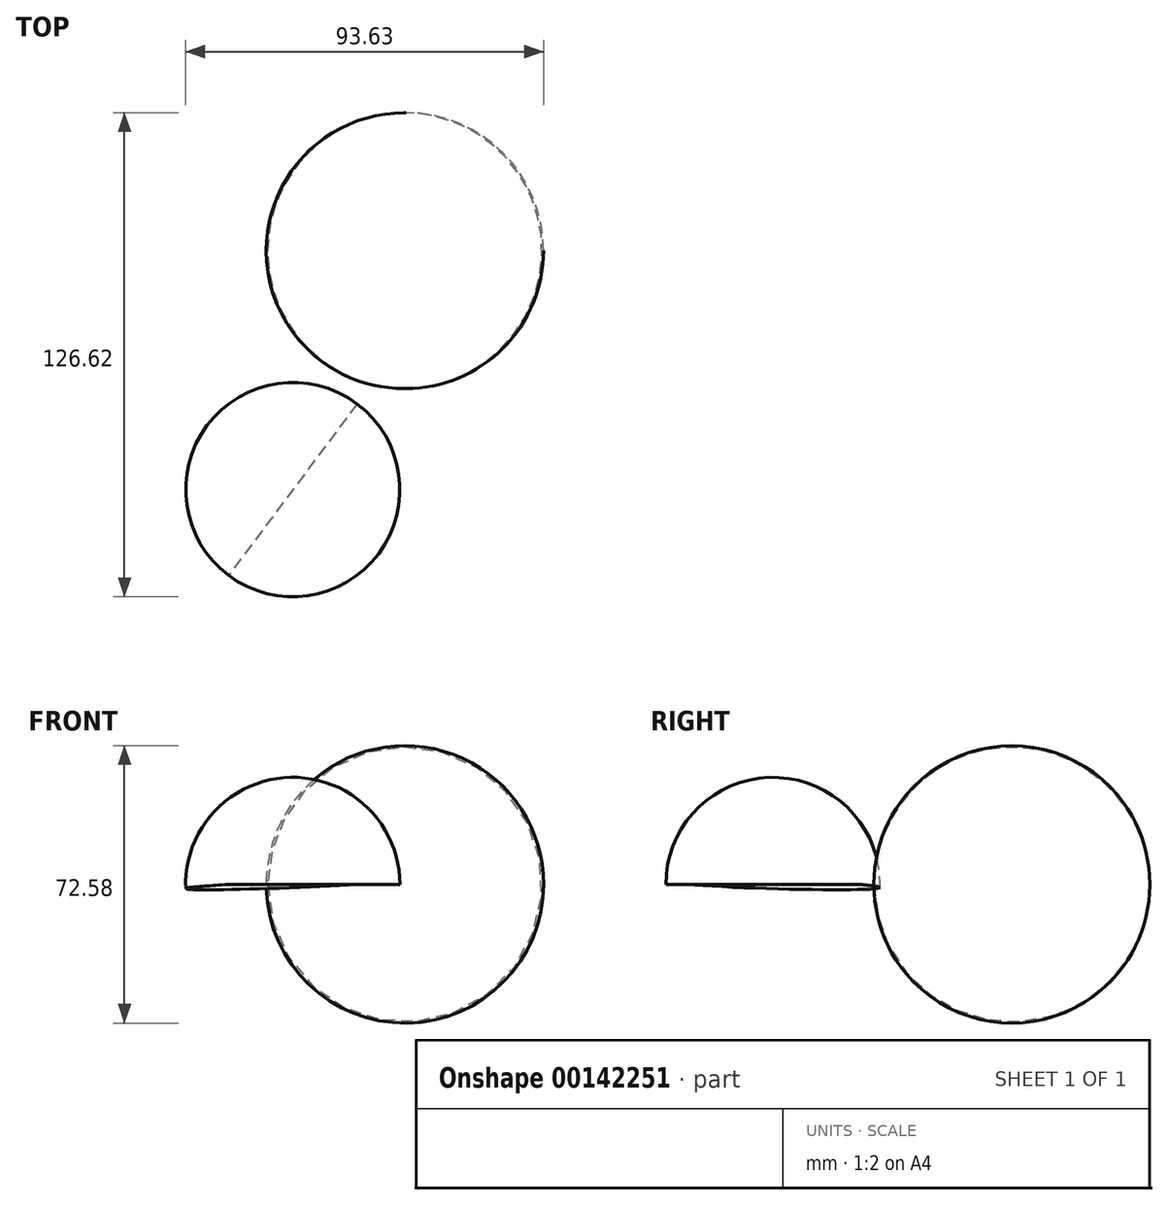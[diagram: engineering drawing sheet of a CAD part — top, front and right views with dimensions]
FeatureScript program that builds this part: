
annotation { "Feature Type Name" : "Feature", "Feature Type Description" : "" }
export const myFeature = defineFeature(function(context is Context, id is Id, definition is map)
    precondition{}
    {
        {
            var Q0;
            Q0=qCreatedBy(makeId("Top.planeOp"),FACE);
            var sketch = newSketch(context, id + "F0", { "sketchPlane" : qUnion([Q0])});
            skCircle(sketch, "E0", {"center": v(-26.35, 26.06) * mm, "radius": 36.08 * mm});
            skLineSegment(sketch, "E1", {"start": v(-26.14, 62.14) * mm, "end": v(-26.14, -10.02) * mm});
            skSolve(sketch);
        }
        {
            var Q0;
            {var subQ0=sQuery(id+"F0.wireOp",EDGE,"E1");Q0=makeQuery(id+"F0.imprint","IMPRINT",FACE,{"disambiguationData":[TD([[makeQuery(id+"F0.imprint","IMPRINT",EDGE,{"derivedFrom":subQ0}),1.0]])]});}
            var Q1;
            Q1=sQuery(id+"F0.wireOp",EDGE,"E1");
            revolve(context, id + "F1", {"entities" : qUnion([Q0]), "axis" : qUnion([Q1]), "revolveType" : RevolveType.FULL, "oppositeDirection" : true});
        }
        {
            var Q0;
            Q0=qCreatedBy(makeId("Top.planeOp"),FACE);
            var sketch = newSketch(context, id + "F2", { "sketchPlane" : qUnion([Q0])});
            skArc(sketch, "E2", {"start": v(-72.27, -58.88) * mm, "mid": v(-33.04, -53.27) * mm, "end": v(-38.66, -14.04) * mm});
            skLineSegment(sketch, "E3", {"start": v(-38.66, -14.04) * mm, "end": v(-72.27, -58.88) * mm});
            skSolve(sketch);
        }
        {
            var Q0;
            Q0=makeQuery(id+"F2.imprint","IMPRINT",FACE,{"disambiguationData":[TD([[makeQuery(id+"F2.imprint","IMPRINT",EDGE,{"derivedFrom":sQuery(id+"F2.wireOp",EDGE,"E2")}),1.0]])]});
            var Q1;
            Q1=sQuery(id+"F2.wireOp",EDGE,"E3");
            revolve(context, id + "F3", {"entities" : qUnion([Q0]), "axis" : qUnion([Q1]), "revolveType" : RevolveType.ONE_DIRECTION, "angle" : 182.86 * degree});
        }
    });
